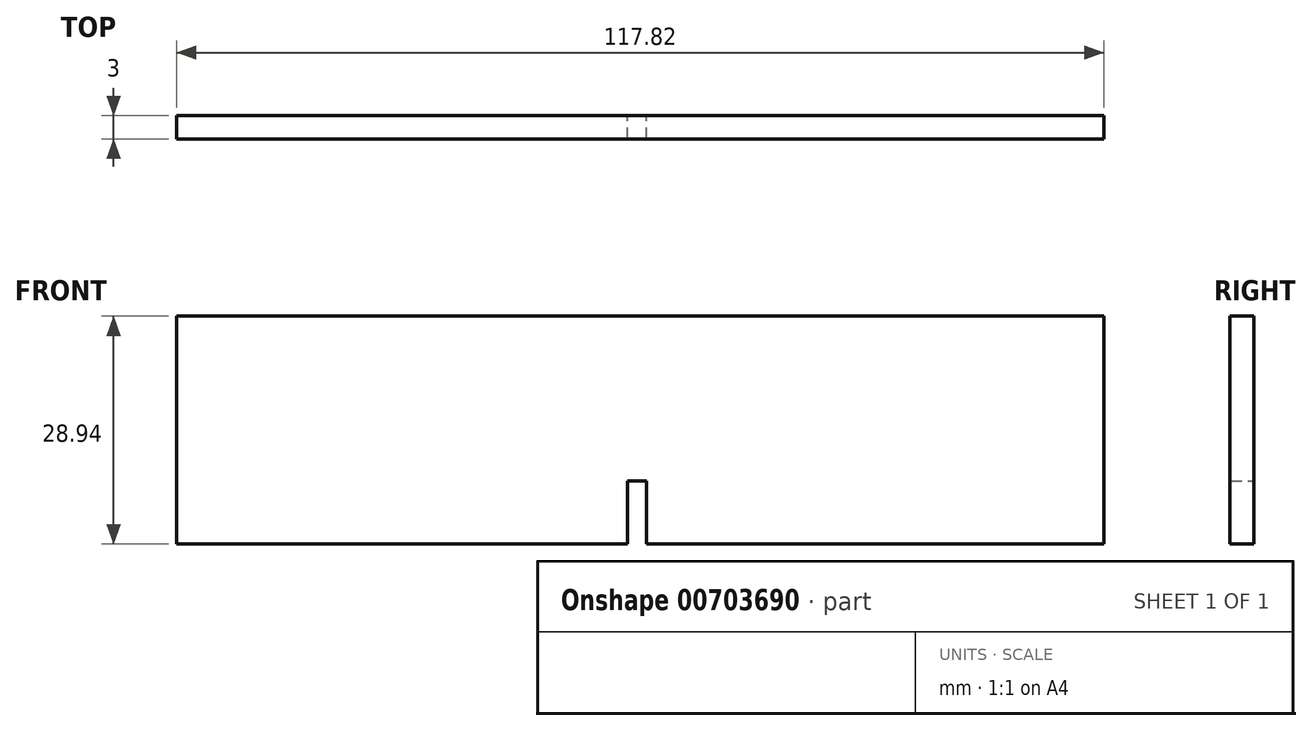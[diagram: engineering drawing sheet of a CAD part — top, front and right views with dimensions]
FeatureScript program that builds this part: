
annotation { "Feature Type Name" : "Feature", "Feature Type Description" : "" }
export const myFeature = defineFeature(function(context is Context, id is Id, definition is map)
    precondition{}
    {
        {
            var Q0;
            Q0=qCreatedBy(makeId("Front.planeOp"),FACE);
            var sketch = newSketch(context, id + "F0", { "sketchPlane" : qUnion([Q0])});
            skLineSegment(sketch, "E0.bottom", {"start": v(-58.5, 14.47) * mm, "end": v(59.32, 14.47) * mm});
            skLineSegment(sketch, "E0.top", {"start": v(-58.5, -14.47) * mm, "end": v(-1.2, -14.47) * mm});
            skLineSegment(sketch, "E0.left", {"start": v(-58.5, 14.47) * mm, "end": v(-58.5, -14.47) * mm});
            skLineSegment(sketch, "E0.right", {"start": v(59.32, 14.47) * mm, "end": v(59.32, -14.47) * mm});
            skLineSegment(sketch, "E1.bottom", {"start": v(1.2, -6.48) * mm, "end": v(-1.2, -6.48) * mm});
            skLineSegment(sketch, "E1.left", {"start": v(1.2, -6.48) * mm, "end": v(1.2, -14.47) * mm});
            skLineSegment(sketch, "E1.right", {"start": v(-1.2, -6.48) * mm, "end": v(-1.2, -14.47) * mm});
            skPoint(sketch, "E1.middle", {"position": v(0, -14.47) * mm});
            skPoint(sketch, "E1.top.start.orphan", {"position": v(1.2, -22.47) * mm});
            skPoint(sketch, "E2.orphan", {"position": v(-1.2, -22.47) * mm});
            skLineSegment(sketch, "E3.trimOffspring", {"start": v(1.2, -14.47) * mm, "end": v(59.32, -14.47) * mm});
            skSolve(sketch);
        }
        {
            var Q0;
            Q0=makeQuery(id+"F0.imprint","IMPRINT",FACE,{"disambiguationData":[TD([[makeQuery(id+"F0.imprint","IMPRINT",EDGE,{"derivedFrom":sQuery(id+"F0.wireOp",EDGE,"E0.bottom")}),-1.0]])]});
            extrude(context, id + "F1", {"entities" : qUnion([Q0]), "depth" : 3 * mm, "offsetDistance" : 25 * mm});
        }
    });
